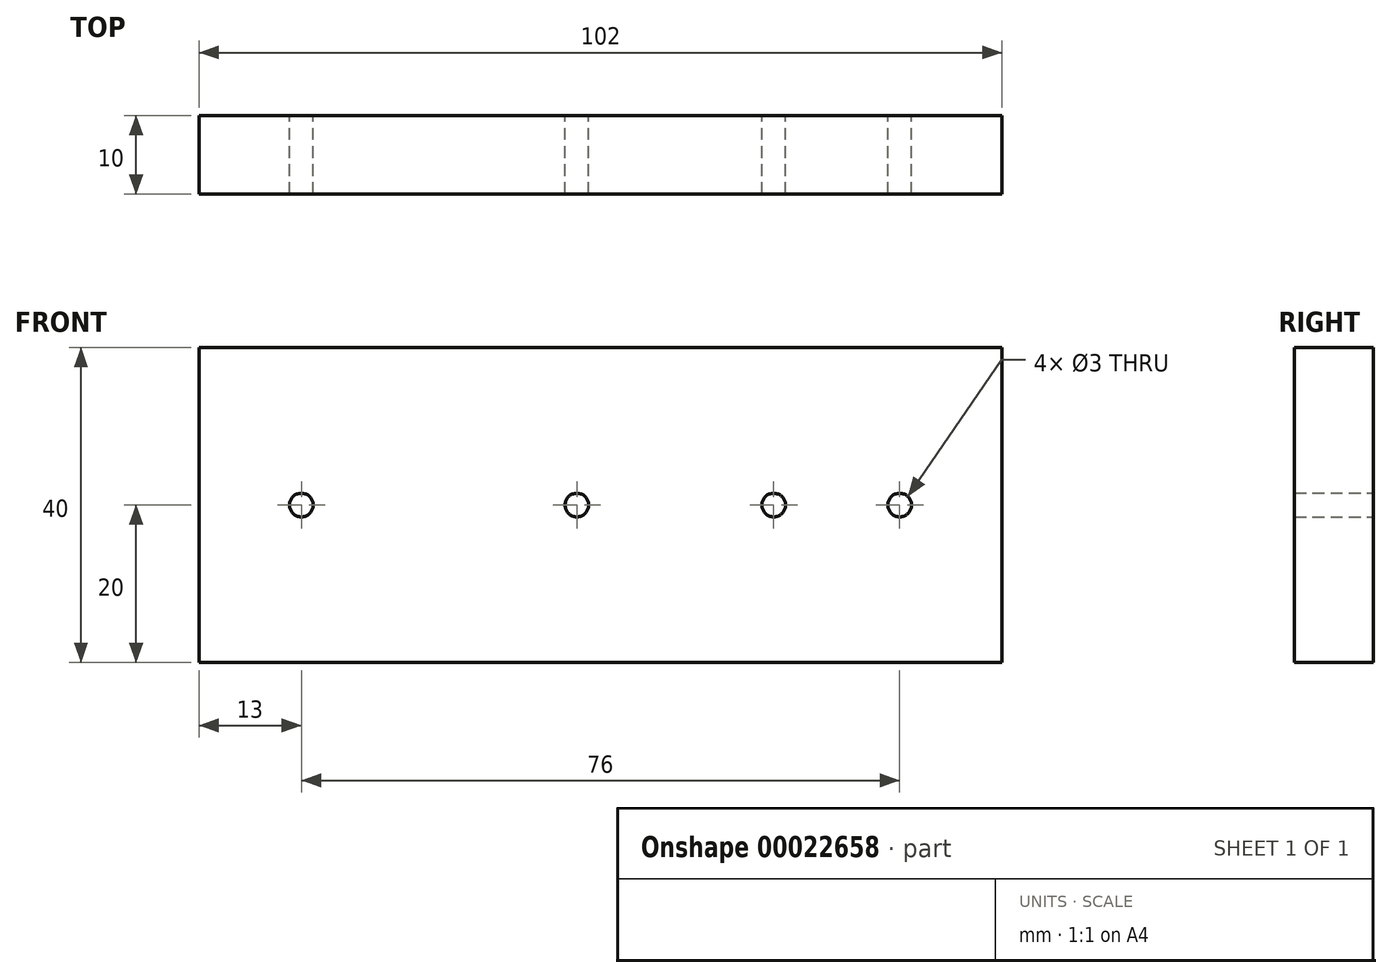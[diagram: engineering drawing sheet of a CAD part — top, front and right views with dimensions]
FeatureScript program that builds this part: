
annotation { "Feature Type Name" : "Feature", "Feature Type Description" : "" }
export const myFeature = defineFeature(function(context is Context, id is Id, definition is map)
    precondition{}
    {
        {
            var Q0;
            Q0=qCreatedBy(makeId("Front.planeOp"),FACE);
            var sketch = newSketch(context, id + "F0", { "sketchPlane" : qUnion([Q0])});
            skLineSegment(sketch, "E0.rect.bottom", {"start": v(-51, 20) * mm, "end": v(51, 20) * mm});
            skLineSegment(sketch, "E0.rect.top", {"start": v(-51, -20) * mm, "end": v(51, -20) * mm});
            skLineSegment(sketch, "E0.rect.left", {"start": v(-51, 20) * mm, "end": v(-51, -20) * mm});
            skLineSegment(sketch, "E0.rect.right", {"start": v(51, 20) * mm, "end": v(51, -20) * mm});
            skPoint(sketch, "E0.rect.middle", {"position": v(0, 0) * mm});
            skCircle(sketch, "E1", {"center": v(-38, 0) * mm, "radius": 1.5 * mm});
            skCircle(sketch, "E2", {"center": v(-3, 0) * mm, "radius": 1.5 * mm});
            skCircle(sketch, "E3", {"center": v(22, 0) * mm, "radius": 1.5 * mm});
            skCircle(sketch, "E4", {"center": v(38, 0) * mm, "radius": 1.5 * mm});
            skSolve(sketch);
        }
        {
            var Q0;
            Q0=makeQuery(id+"F0.imprint","IMPRINT",FACE,{"disambiguationData":[TD([[makeQuery(id+"F0.imprint","IMPRINT",EDGE,{"derivedFrom":sQuery(id+"F0.wireOp",EDGE,"E0.rect.bottom")}),-1.0]])]});
            extrude(context, id + "F1", {"entities" : qUnion([Q0]), "depth" : 10 * mm});
        }
    });
